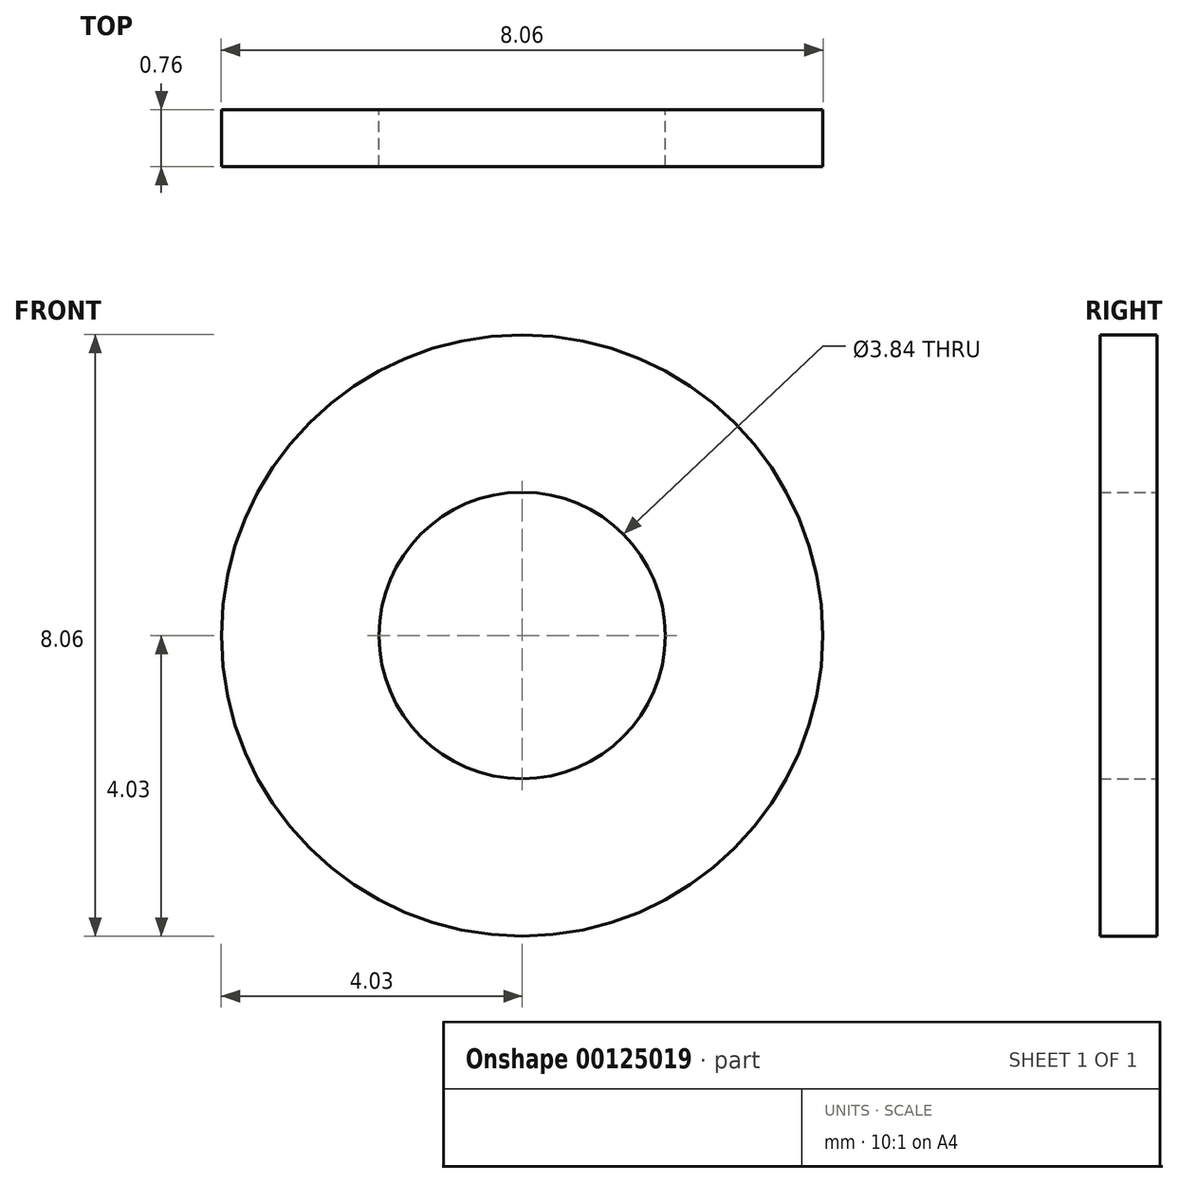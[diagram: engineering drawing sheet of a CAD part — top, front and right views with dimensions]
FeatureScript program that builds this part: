
annotation { "Feature Type Name" : "Feature", "Feature Type Description" : "" }
export const myFeature = defineFeature(function(context is Context, id is Id, definition is map)
    precondition{}
    {
        {
            var Q0;
            Q0=qCreatedBy(makeId("Front.planeOp"),FACE);
            var sketch = newSketch(context, id + "F0", { "sketchPlane" : qUnion([Q0])});
            skCircle(sketch, "E0", {"center": v(0, 0) * mm, "radius": 4.03 * mm});
            skPoint(sketch, "E0.first.point", {"position": v(-4.03, 0) * mm});
            skPoint(sketch, "E0.second.point", {"position": v(3, -2.7) * mm});
            skPoint(sketch, "E0.third.point", {"position": v(2.78, 2.91) * mm});
            skCircle(sketch, "E1", {"center": v(0, 0) * mm, "radius": 1.92 * mm});
            skPoint(sketch, "E1.first.point", {"position": v(1.92, 0) * mm});
            skPoint(sketch, "E1.second.point", {"position": v(-1.92, 0) * mm});
            skPoint(sketch, "E1.third.point", {"position": v(0, 1.92) * mm});
            skSolve(sketch);
        }
        {
            var Q0;
            Q0=qCreatedBy(makeId("Right.planeOp"),FACE);
            var sketch = newSketch(context, id + "F1", { "sketchPlane" : qUnion([Q0])});
            skLineSegment(sketch, "E2", {"start": v(0, 0) * mm, "end": v(0.76, 0) * mm});
            skSolve(sketch);
        }
        {
            var Q0;
            Q0=makeQuery(id+"F0.imprint","IMPRINT",FACE,{"disambiguationData":[TD([[makeQuery(id+"F0.imprint","IMPRINT",EDGE,{"derivedFrom":sQuery(id+"F0.wireOp",EDGE,"E0")}),1.0]])]});
            var Q1;
            Q1=sQuery(id+"F1.wireOp",EDGE,"E2");
            sweep(context, id + "F2", {"profiles" : qUnion([Q0]), "path" : qUnion([Q1])});
        }
    });
